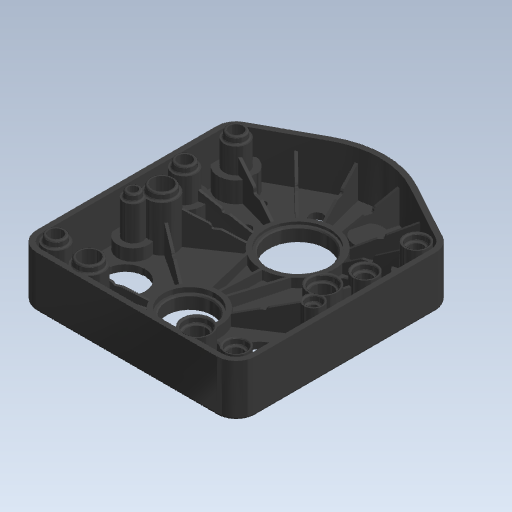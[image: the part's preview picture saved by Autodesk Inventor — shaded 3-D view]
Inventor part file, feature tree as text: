
AUTODESK INVENTOR PART (.ipt)
format: ipt  version: 2020 (Build 240168000, 168)  size: 668,160 bytes
history: native  units: mm (DEFAULTED — no unit token found)
features: fillet x1
ambient origin geometry x8: Origin, YZ Plane, XZ Plane, XY Plane, X Axis, Y Axis, Z Axis, Center Point
bodies: Solid1 (feature_tree)
feature tree (1):
  fillet  "Fillet18"  [1 undecoded]
note: 1 required parameter value undecoded (feature->parameter linkage not recoverable at this tier; creation-order binding heuristic only, values carry confidence <= 0.55)
